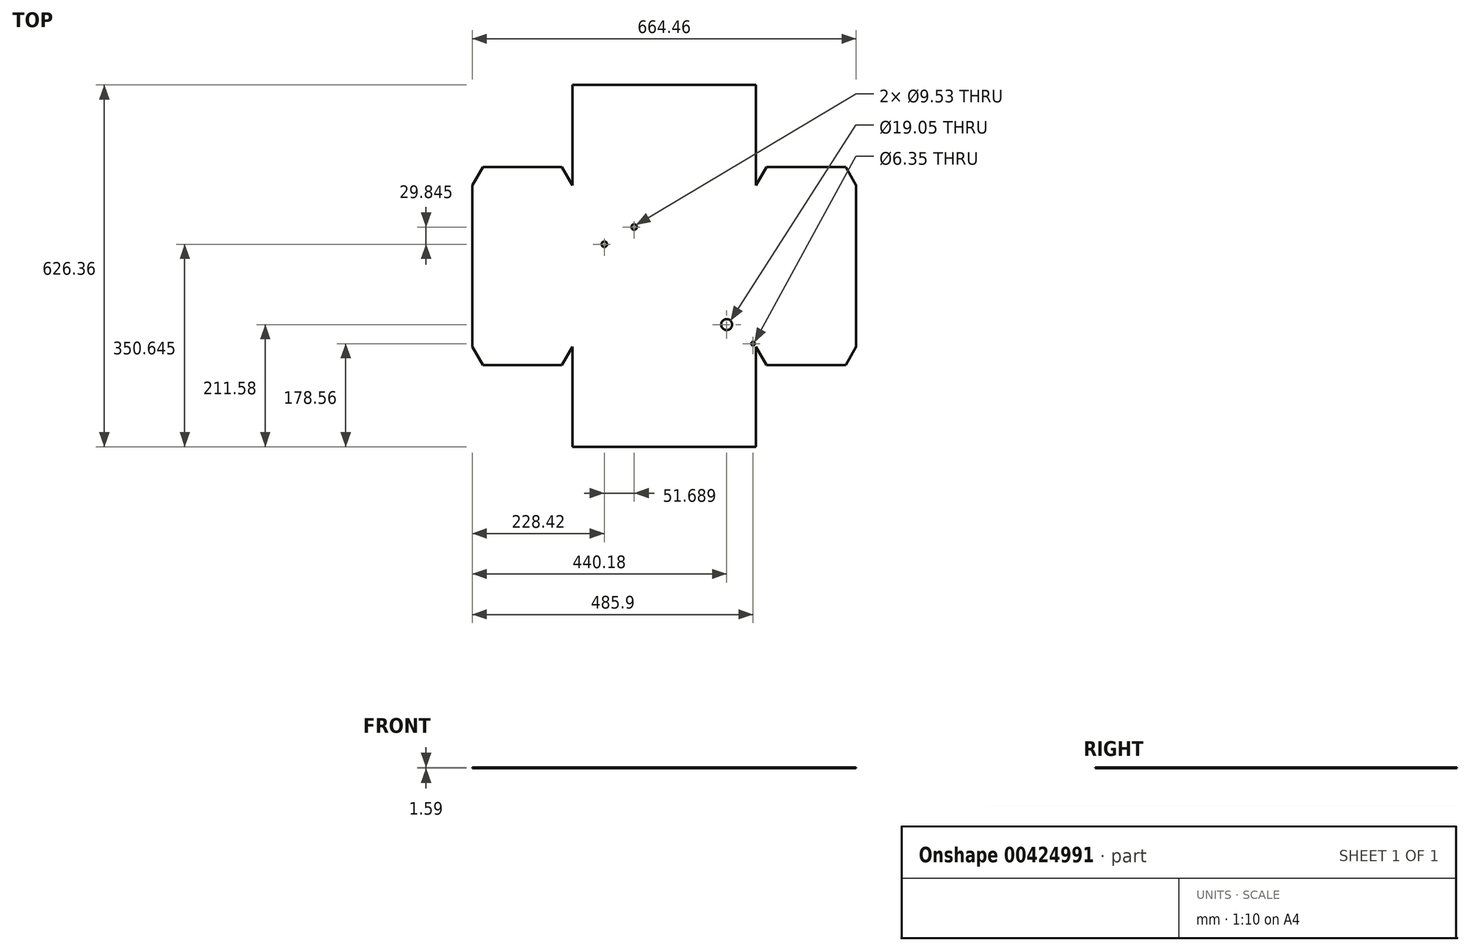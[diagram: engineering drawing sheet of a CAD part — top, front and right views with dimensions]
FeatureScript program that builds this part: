
annotation { "Feature Type Name" : "Feature", "Feature Type Description" : "" }
export const myFeature = defineFeature(function(context is Context, id is Id, definition is map)
    precondition{}
    {
        {
            var Q0;
            Q0=qCreatedBy(makeId("Top.planeOp"),FACE);
            var sketch = newSketch(context, id + "F0", { "sketchPlane" : qUnion([Q0])});
            skLineSegment(sketch, "E0.bottom", {"start": v(158.75, -139.7) * mm, "end": v(-158.75, -139.7) * mm});
            skLineSegment(sketch, "E0.top", {"start": v(158.75, 139.7) * mm, "end": v(-158.75, 139.7) * mm});
            skLineSegment(sketch, "E0.left", {"start": v(158.75, -139.7) * mm, "end": v(158.75, 139.7) * mm});
            skLineSegment(sketch, "E0.right", {"start": v(-158.75, -139.7) * mm, "end": v(-158.75, 139.7) * mm});
            skPoint(sketch, "E0.middle", {"position": v(0, 0) * mm});
            skLineSegment(sketch, "E1", {"start": v(158.75, -139.7) * mm, "end": v(332.23, -139.7) * mm});
            skLineSegment(sketch, "E2", {"start": v(332.23, -139.7) * mm, "end": v(332.23, 139.7) * mm});
            skLineSegment(sketch, "E3", {"start": v(332.23, 139.7) * mm, "end": v(158.75, 139.7) * mm});
            skLineSegment(sketch, "E4", {"start": v(-158.75, -139.7) * mm, "end": v(-158.75, -313.18) * mm});
            skLineSegment(sketch, "E5", {"start": v(-158.75, -313.18) * mm, "end": v(158.75, -313.18) * mm});
            skLineSegment(sketch, "E6", {"start": v(158.75, -313.18) * mm, "end": v(158.75, -139.7) * mm});
            skLineSegment(sketch, "E7", {"start": v(-158.75, -139.7) * mm, "end": v(-332.23, -139.7) * mm});
            skLineSegment(sketch, "E8", {"start": v(-332.23, -139.7) * mm, "end": v(-332.23, 139.7) * mm});
            skLineSegment(sketch, "E9", {"start": v(-332.23, 139.7) * mm, "end": v(-158.75, 139.7) * mm});
            skLineSegment(sketch, "E10", {"start": v(-158.75, 139.7) * mm, "end": v(-158.75, 313.18) * mm});
            skLineSegment(sketch, "E11", {"start": v(158.75, 313.18) * mm, "end": v(158.75, 139.7) * mm});
            skLineSegment(sketch, "E12", {"start": v(158.75, 313.18) * mm, "end": v(-158.75, 313.18) * mm});
            skLineSegment(sketch, "E13", {"start": v(158.75, -139.7) * mm, "end": v(177.08, -171.45) * mm});
            skLineSegment(sketch, "E14", {"start": v(177.08, -171.45) * mm, "end": v(313.9, -171.45) * mm});
            skLineSegment(sketch, "E15", {"start": v(313.9, -171.45) * mm, "end": v(332.23, -139.7) * mm});
            skLineSegment(sketch, "E16", {"start": v(-332.23, -139.7) * mm, "end": v(-313.9, -171.45) * mm});
            skLineSegment(sketch, "E17", {"start": v(-313.9, -171.45) * mm, "end": v(-177.08, -171.45) * mm});
            skLineSegment(sketch, "E18", {"start": v(-177.08, -171.45) * mm, "end": v(-158.75, -139.7) * mm});
            skLineSegment(sketch, "E19", {"start": v(-332.23, 139.7) * mm, "end": v(-313.9, 171.45) * mm});
            skLineSegment(sketch, "E20", {"start": v(-313.9, 171.45) * mm, "end": v(-177.08, 171.45) * mm});
            skLineSegment(sketch, "E21", {"start": v(-177.08, 171.45) * mm, "end": v(-158.75, 139.7) * mm});
            skLineSegment(sketch, "E22", {"start": v(158.75, 139.7) * mm, "end": v(177.08, 171.45) * mm});
            skLineSegment(sketch, "E23", {"start": v(177.08, 171.45) * mm, "end": v(313.9, 171.45) * mm});
            skLineSegment(sketch, "E24", {"start": v(313.9, 171.45) * mm, "end": v(332.23, 139.7) * mm});
            skCircle(sketch, "E25", {"center": v(-103.8, 37.46) * mm, "radius": 4.76 * mm});
            skCircle(sketch, "E26", {"center": v(-52.12, 67.3) * mm, "radius": 4.76 * mm});
            skCircle(sketch, "E27", {"center": v(107.95, -101.6) * mm, "radius": 9.53 * mm});
            skCircle(sketch, "E28", {"center": v(153.67, -134.62) * mm, "radius": 3.18 * mm});
            skSolve(sketch);
        }
        {
            var Q0;
            Q0=makeQuery(id+"F0.imprint","IMPRINT",FACE,{"disambiguationData":[TD([[makeQuery(id+"F0.imprint","IMPRINT",EDGE,{"derivedFrom":sQuery(id+"F0.wireOp",EDGE,"E0.top")}),-1.0]])]});
            var Q1;
            Q1=makeQuery(id+"F0.imprint","IMPRINT",FACE,{"disambiguationData":[TD([[makeQuery(id+"F0.imprint","IMPRINT",EDGE,{"derivedFrom":sQuery(id+"F0.wireOp",EDGE,"E9")}),1.0]])]});
            var Q2;
            Q2=makeQuery(id+"F0.imprint","IMPRINT",FACE,{"disambiguationData":[TD([[makeQuery(id+"F0.imprint","IMPRINT",EDGE,{"derivedFrom":sQuery(id+"F0.wireOp",EDGE,"E0.right")}),1.0]])]});
            var Q3;
            Q3=makeQuery(id+"F0.imprint","IMPRINT",FACE,{"disambiguationData":[TD([[makeQuery(id+"F0.imprint","IMPRINT",EDGE,{"derivedFrom":sQuery(id+"F0.wireOp",EDGE,"E7")}),1.0]])]});
            var Q4;
            Q4=makeQuery(id+"F0.imprint","IMPRINT",FACE,{"disambiguationData":[TD([[makeQuery(id+"F0.imprint","IMPRINT",EDGE,{"derivedFrom":sQuery(id+"F0.wireOp",EDGE,"E0.bottom")}),1.0]])]});
            var Q5;
            Q5=makeQuery(id+"F0.imprint","IMPRINT",FACE,{"disambiguationData":[TD([[makeQuery(id+"F0.imprint","IMPRINT",EDGE,{"derivedFrom":sQuery(id+"F0.wireOp",EDGE,"E0.bottom")}),-1.0]])]});
            var Q6;
            Q6=makeQuery(id+"F0.imprint","IMPRINT",FACE,{"disambiguationData":[TD([[makeQuery(id+"F0.imprint","IMPRINT",EDGE,{"derivedFrom":sQuery(id+"F0.wireOp",EDGE,"E0.left")}),-1.0]])]});
            var Q7;
            Q7=makeQuery(id+"F0.imprint","IMPRINT",FACE,{"disambiguationData":[TD([[makeQuery(id+"F0.imprint","IMPRINT",EDGE,{"derivedFrom":sQuery(id+"F0.wireOp",EDGE,"E1")}),-1.0]])]});
            var Q8;
            Q8=makeQuery(id+"F0.imprint","IMPRINT",FACE,{"disambiguationData":[TD([[makeQuery(id+"F0.imprint","IMPRINT",EDGE,{"derivedFrom":sQuery(id+"F0.wireOp",EDGE,"E3")}),-1.0]])]});
            extrude(context, id + "F1", {"entities" : qUnion([Q0, Q1, Q2, Q3, Q4, Q5, Q6, Q7, Q8]), "depth" : 1.59 * mm});
        }
    });
